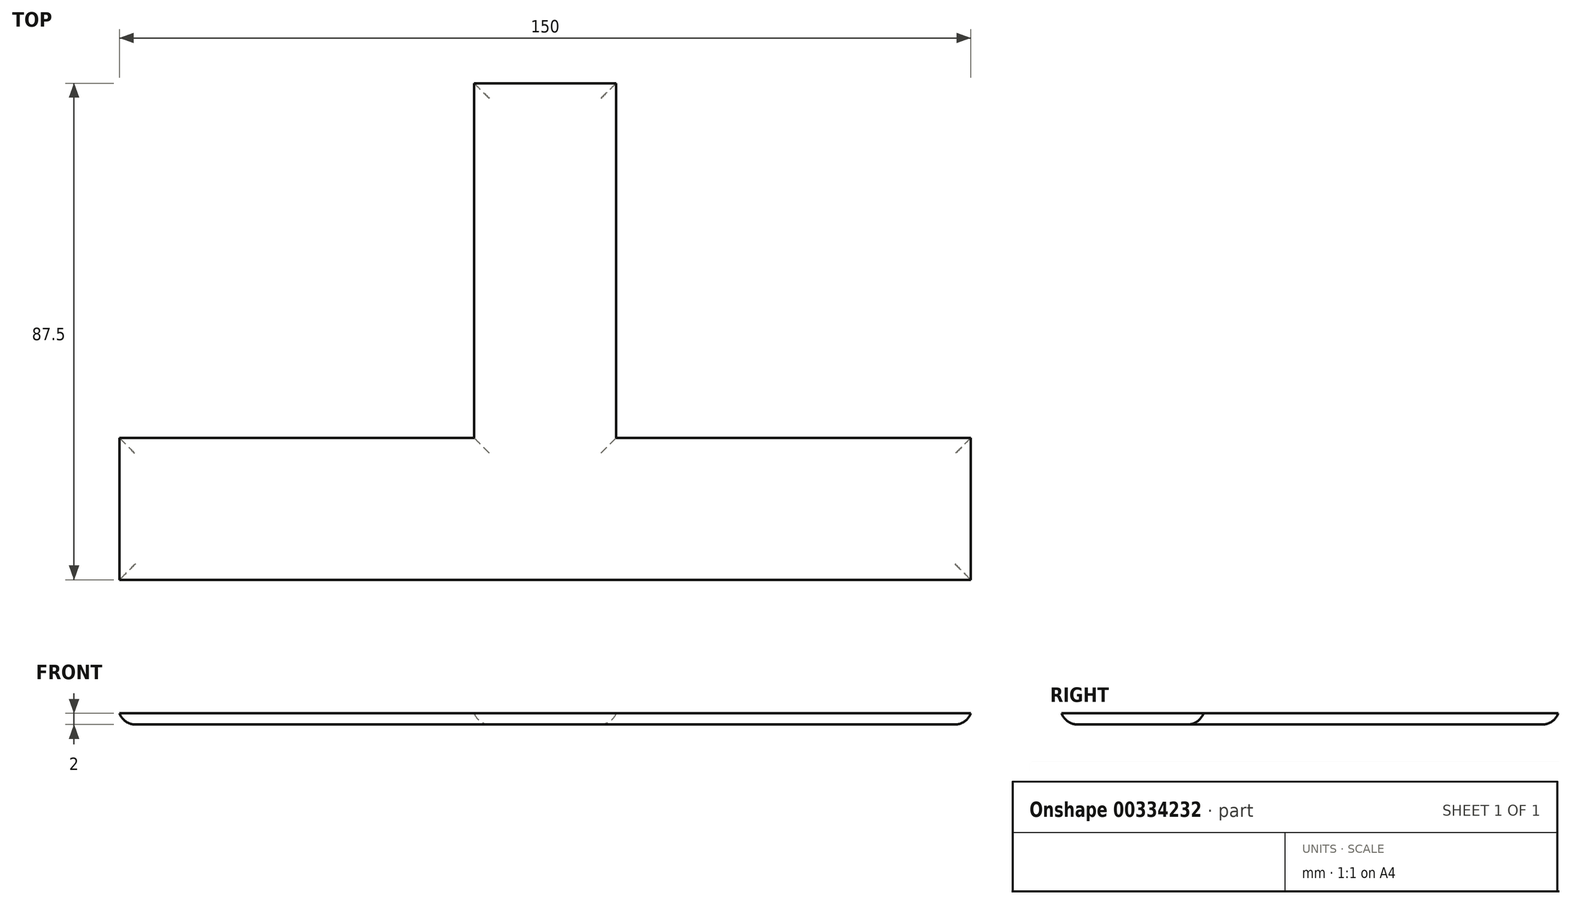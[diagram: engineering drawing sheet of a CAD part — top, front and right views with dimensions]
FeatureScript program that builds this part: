
annotation { "Feature Type Name" : "Feature", "Feature Type Description" : "" }
export const myFeature = defineFeature(function(context is Context, id is Id, definition is map)
    precondition{}
    {
        {
            var Q0;
            Q0=qCreatedBy(makeId("Top.planeOp"),FACE);
            var sketch = newSketch(context, id + "F0", { "sketchPlane" : qUnion([Q0])});
            skLineSegment(sketch, "E0.bottom", {"start": v(12.5, -75) * mm, "end": v(-12.5, -75) * mm});
            skLineSegment(sketch, "E0.top", {"start": v(12.5, 75) * mm, "end": v(-12.5, 75) * mm});
            skLineSegment(sketch, "E0.left", {"start": v(12.5, -75) * mm, "end": v(12.5, 75) * mm});
            skLineSegment(sketch, "E0.right", {"start": v(-12.5, -75) * mm, "end": v(-12.5, 75) * mm});
            skPoint(sketch, "E0.middle", {"position": v(0, 0) * mm});
            skLineSegment(sketch, "E1.bottom", {"start": v(75, -12.5) * mm, "end": v(-75, -12.5) * mm});
            skLineSegment(sketch, "E1.top", {"start": v(75, 12.5) * mm, "end": v(-75, 12.5) * mm});
            skLineSegment(sketch, "E1.left", {"start": v(75, -12.5) * mm, "end": v(75, 12.5) * mm});
            skLineSegment(sketch, "E2.bottom", {"start": v(-12.5, -75) * mm, "end": v(12.5, -75) * mm});
            skLineSegment(sketch, "E3.left", {"start": v(-75, 12.5) * mm, "end": v(-75, -12.5) * mm});
            skSolve(sketch);
        }
        {
            var Q0;
            {var subQ0=sQuery(id+"F0.wireOp",EDGE,"HU53E8sc-iPn4-ztWB-7ShW-lq6fokxsmWkS.bottom");Q0=makeQuery(id+"F0.imprint","IMPRINT",FACE,{"disambiguationData":[TD([[makeQuery(id+"F0.imprint","IMPRINT",EDGE,{"derivedFrom":subQ0}),-1.0]])]});}
            var Q1;
            {var subQ5=sQuery(id+"F0.wireOp",EDGE,"E3.left");Q1=makeQuery(id+"F0.imprint","IMPRINT",FACE,{"disambiguationData":[TD([[makeQuery(id+"F0.imprint","IMPRINT",EDGE,{"derivedFrom":subQ5}),1.0]])]});}
            var Q2;
            {var subQ0=sQuery(id+"F0.wireOp",EDGE,"E1.bottom");var subQ1=sQuery(id+"F0.wireOp",EDGE,"E0.left");var subQ2=makeQuery(id+"F0.imprint","INTERSECT",VERTEX,{"derivedFrom":[subQ1,subQ0]});Q2=makeQuery(id+"F0.imprint","IMPRINT",FACE,{"disambiguationData":[TD([[makeQuery(id+"F0.imprint","IMPRINT",EDGE,{"disambiguationData":[TD([[subQ2,-1.0]])],"derivedFrom":subQ1}),1.0]])]});}
            var Q3;
            {var subQ5=sQuery(id+"F0.wireOp",EDGE,"Z96oht9U-KK9e-jwxB-IJ0v-EqWNfPS5vhPp.left");Q3=makeQuery(id+"F0.imprint","IMPRINT",FACE,{"disambiguationData":[TD([[makeQuery(id+"F0.imprint","IMPRINT",EDGE,{"derivedFrom":subQ5}),-1.0]])]});}
            var Q4;
            {var subQ0=sQuery(id+"F0.wireOp",EDGE,"E2.bottom");Q4=makeQuery(id+"F0.imprint","IMPRINT",FACE,{"disambiguationData":[TD([[makeQuery(id+"F0.imprint","IMPRINT",EDGE,{"derivedFrom":subQ0}),1.0]])]});}
            var Q5;
            {var subQ0=sQuery(id+"F0.wireOp",EDGE,"E0.top");Q5=makeQuery(id+"F0.imprint","IMPRINT",FACE,{"disambiguationData":[TD([[makeQuery(id+"F0.imprint","IMPRINT",EDGE,{"derivedFrom":subQ0}),1.0]])]});}
            var Q6;
            {var subQ5=sQuery(id+"F0.wireOp",EDGE,"E1.left");Q6=makeQuery(id+"F0.imprint","IMPRINT",FACE,{"disambiguationData":[TD([[makeQuery(id+"F0.imprint","IMPRINT",EDGE,{"derivedFrom":subQ5}),1.0]])]});}
            extrude(context, id + "F1", {"entities" : qUnion([Q0, Q1, Q2, Q3, Q4, Q5, Q6]), "depth" : 2 * mm});
        }
        {
            var Q0;
            Q0=makeQuery(id+"F1.opExtrude","CAP_FACE",FACE,{"disambiguationData":[OSD([sQuery(id+"F0.wireOp",EDGE,"E0.top"),sQuery(id+"F0.wireOp",EDGE,"E0.left"),sQuery(id+"F0.wireOp",EDGE,"E0.right"),sQuery(id+"F0.wireOp",EDGE,"E1.bottom"),sQuery(id+"F0.wireOp",EDGE,"E1.top"),sQuery(id+"F0.wireOp",EDGE,"E1.left"),sQuery(id+"F0.wireOp",EDGE,"E2.bottom"),sQuery(id+"F0.wireOp",EDGE,"E3.left")])],"isStart":true});
            fillet(context, id + "F2", {"entities" : qUnion([Q0]), "radius" : 3 * mm, "tangentPropagation" : true, "allowEdgeOverflow" : false});
        }
    });
